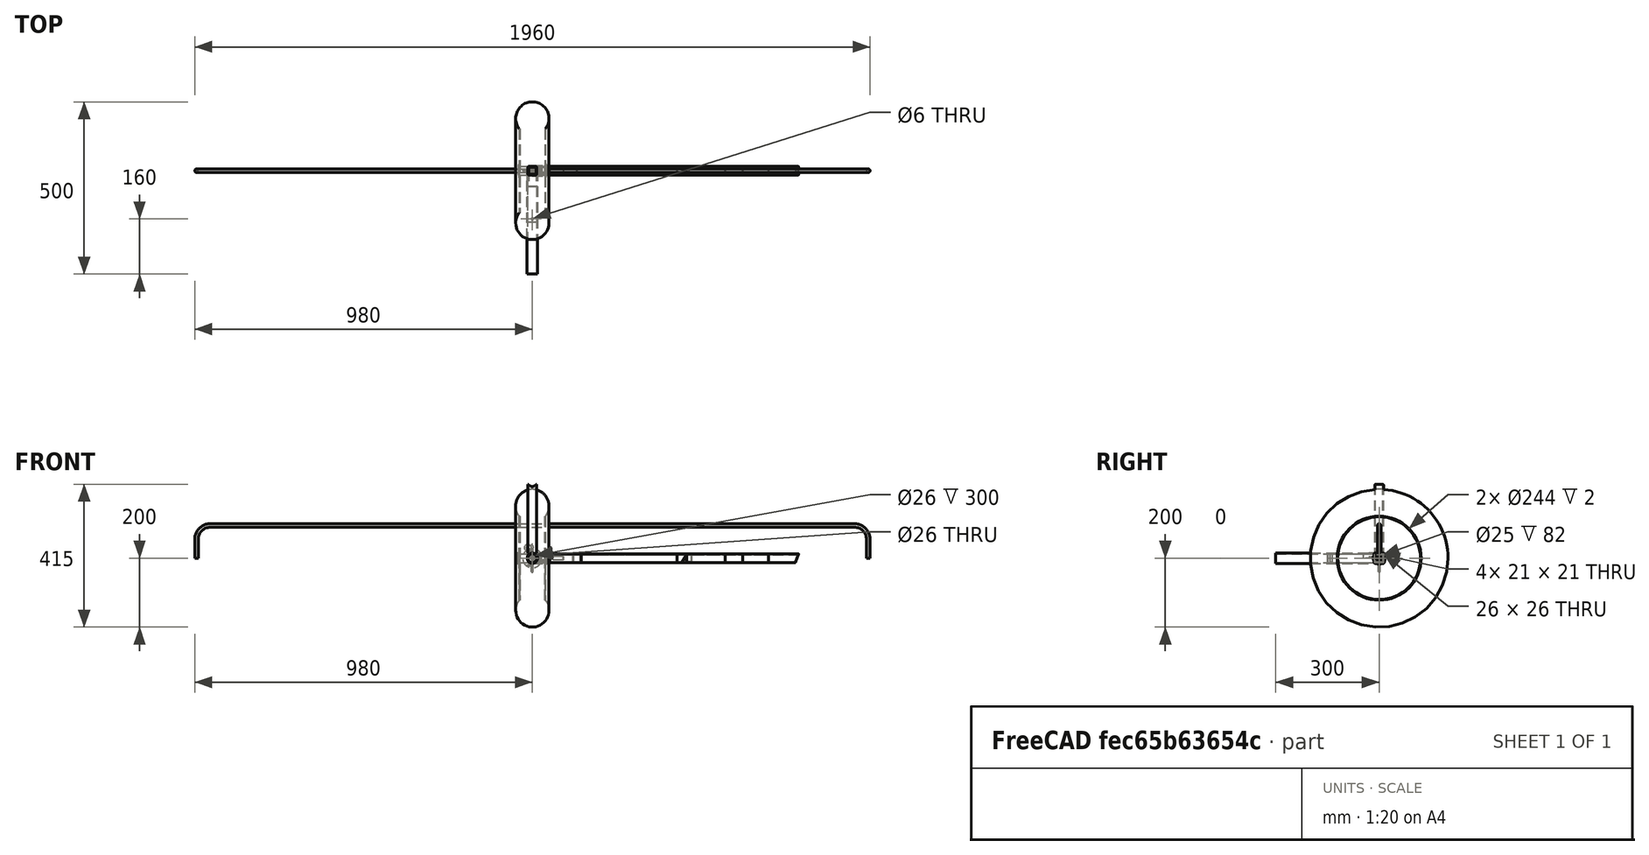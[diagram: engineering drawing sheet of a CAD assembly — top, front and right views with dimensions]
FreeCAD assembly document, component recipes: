
FREECAD ASSEMBLY — COMPONENT RECIPES ("brouetteas4-am")

This assembly document has 25 components, labeled P0..P24 below (a component is one placed body or linked part). 24 of them carry a construction recipe — the FreeCAD feature program that regenerates the part from scratch, quoted from this document or its linked companion documents; the rest are supplied as boundary geometry only. No exploded tour is included for this assembly.
COMPONENT P0 — recipe-attached ("A1", modeled in this document).
Construction recipe (the document's own serialized feature program — sketch geometry with constraints, then the solid features built on it; lengths are millimeters unless a unit is written):

FEATURE [PartDesign::Body] A1005
  AllowCompound = false
  Origin = -> Origin015
COMPONENT P1 — recipe-attached ("A2", modeled in this document).
Construction recipe (the document's own serialized feature program — sketch geometry with constraints, then the solid features built on it; lengths are millimeters unless a unit is written):

FEATURE [PartDesign::Body] Body001
  AllowCompound = false
  Origin = -> Origin004
COMPONENT P2 — recipe-attached ("A3", modeled in this document).
Construction recipe (the document's own serialized feature program — sketch geometry with constraints, then the solid features built on it; lengths are millimeters unless a unit is written):

FEATURE [Sketcher::SketchObject] Sketch002
  ArcFitTolerance = 0
  AttachmentSupport = -> [XZ_Plane007]
  FullyConstrained = true
  MakeInternals = false
  MapMode = 5
  Placement = pos=(0,0,0) rot=(1,0,0;1.5708rad)
  expr: .Constraints.longueur = Spreadsheet.B4 - Spreadsheet.B2 * 2 - 10
  expr: Constraints[4] = Spreadsheet.B2
  sketch-geometry (7):
    g0: LineSegment StartX=-975 StartY=0 StartZ=0 EndX=-975 EndY=25 EndZ=0
    g1: LineSegment StartX=975 StartY=8e-16 StartZ=0 EndX=975 EndY=25 EndZ=0
    g2: LineSegment StartX=-975 StartY=25 StartZ=0 EndX=-975 EndY=55 EndZ=0
    g3: LineSegment StartX=-935 StartY=95 StartZ=0 EndX=935 EndY=95 EndZ=0
    g4: LineSegment StartX=975 StartY=55 StartZ=0 EndX=975 EndY=25 EndZ=0
    g5: ArcOfCircle CenterX=935 CenterY=55 CenterZ=0 NormalX=0 NormalY=0 NormalZ=1 AngleXU=0 Radius=40 StartAngle=0 EndAngle=1.5708
    g6: ArcOfCircle CenterX=-935 CenterY=55 CenterZ=0 NormalX=0 NormalY=0 NormalZ=1 AngleXU=0 Radius=40 StartAngle=1.5708 EndAngle=3.14159
  constraints (19):
    c: PointOnObject(g0,g-1)
    c: Vertical(g0)
    c: Vertical(g1)
    c: Symmetric(g0,g1,g-2)
    c: DistanceY(g0,g0) = 25
    c: DistanceX(g0,g1) = 1950  'longueur'
    c: Equal(g1,g0)
    c: Coincident(g0,g2)
    c: Vertical(g2)
    c: Horizontal(g3)
    c: Coincident(g4,g1)
    c: Vertical(g4)
    c: Tangent(g3,g5) = 1.5708
    c: Tangent(g4,g5) = 1.5708
    c: Tangent(g2,g6) = 1.5708
    c: Tangent(g3,g6) = 1.5708
    c: Equal(g6,g5)
    c: DistanceY(g0,g3) = 70
    c: Radius(g6) = 40
FEATURE [Sketcher::SketchObject] Sketch003
  ArcFitTolerance = 0
  AttachmentSupport = -> [XY_Plane007]
  ExternalGeometry = -> [Sketch002]
  FullyConstrained = true
  MakeInternals = false
  MapMode = 5
  sketch-geometry (1):
    g0: Circle CenterX=-975 CenterY=0 CenterZ=0 NormalX=0 NormalY=0 NormalZ=1 AngleXU=0 Radius=5
  constraints (2):
    c: Coincident(g0,g-3)
    c: Diameter(g0) = 10
FEATURE [PartDesign::AdditivePipe] AdditivePipe
  AuxilleryCurvelinear = true
  AuxillerySpineTangent = false
  Binormal = (0,0,0)
  Mode = 0
  Profile = -> Sketch003
  Spine = -> Sketch002
  SpineTangent = false
  Suppressed = false
  Transformation = 0
  Transition = 0
FEATURE [PartDesign::Body] Body002
  AllowCompound = false
  Group = -> [Sketch002,Sketch003,AdditivePipe]
  Origin = -> Origin007
  Tip = -> AdditivePipe
COMPONENT P3 — recipe-attached ("A4", modeled in this document).
Construction recipe (the document's own serialized feature program — sketch geometry with constraints, then the solid features built on it; lengths are millimeters unless a unit is written):

FEATURE [Sketcher::SketchObject] Sketch004
  ArcFitTolerance = 0
  AttachmentSupport = -> [YZ_Plane008]
  FullyConstrained = true
  MakeInternals = false
  MapMode = 5
  Placement = pos=(0,0,0) rot=(0.57735,0.57735,0.57735;2.0944rad)
  sketch-geometry (1):
    g0: Circle CenterX=0 CenterY=0 CenterZ=0 NormalX=0 NormalY=0 NormalZ=1 AngleXU=0 Radius=5
  constraints (2):
    c: Coincident(g0,g-1)
    c: Diameter(g0) = 10  'diametre'
FEATURE [PartDesign::Pad] Pad002
  Direction = (1,0,0)
  Length = 90
  Length2 = 100
  Placement = pos=(0,0,0) rot=(0.57735,0.57735,0.57735;2.0944rad)
  Profile = -> Sketch004
  Suppressed = false
  Type = 0
FEATURE [PartDesign::Body] Body003
  AllowCompound = false
  Group = -> [Sketch004,Pad002]
  Origin = -> Origin008
  Tip = -> Pad002
COMPONENT P4 — recipe-attached ("A5", modeled in this document).
Construction recipe (the document's own serialized feature program — sketch geometry with constraints, then the solid features built on it; lengths are millimeters unless a unit is written):

FEATURE [PartDesign::Body] Body005
  AllowCompound = false
  Origin = -> Origin012
COMPONENT P5 — recipe-attached ("A6", modeled in this document).
Construction recipe (the document's own serialized feature program — sketch geometry with constraints, then the solid features built on it; lengths are millimeters unless a unit is written):

FEATURE [Sketcher::SketchObject] Sketch008
  ArcFitTolerance = 0
  FullyConstrained = true
  MakeInternals = false
  MapMode = 2
  Placement = pos=(0,0,0) rot=(0.57735,0.57735,0.57735;2.0944rad)
  expr: Constraints[15] = .Constraints.hauteur * 0.1
  expr: Constraints[27] = .Constraints.epaisseur
  sketch-geometry (12):
    g0: LineSegment StartX=-10 StartY=12.5 StartZ=0 EndX=10 EndY=12.5 EndZ=0
    g1: LineSegment StartX=12.5 StartY=10 StartZ=0 EndX=12.5 EndY=-10 EndZ=0
    g2: LineSegment StartX=10 StartY=-12.5 StartZ=0 EndX=-10 EndY=-12.5 EndZ=0
    g3: LineSegment StartX=-12.5 StartY=-10 StartZ=0 EndX=-12.5 EndY=10 EndZ=0
    g4: ArcOfCircle CenterX=-10 CenterY=10 CenterZ=0 NormalX=0 NormalY=0 NormalZ=1 AngleXU=0 Radius=2.5 StartAngle=1.5708 EndAngle=3.14159
    g5: ArcOfCircle CenterX=10 CenterY=10 CenterZ=0 NormalX=0 NormalY=0 NormalZ=1 AngleXU=0 Radius=2.5 StartAngle=2e-16 EndAngle=1.5708
    g6: ArcOfCircle CenterX=10 CenterY=-10 CenterZ=0 NormalX=0 NormalY=0 NormalZ=1 AngleXU=0 Radius=2.5 StartAngle=4.71239 EndAngle=6.28319
    g7: ArcOfCircle CenterX=-10 CenterY=-10 CenterZ=0 NormalX=0 NormalY=0 NormalZ=1 AngleXU=0 Radius=2.5 StartAngle=3.14159 EndAngle=4.71239
    g8: LineSegment StartX=-10.5 StartY=10.5 StartZ=0 EndX=10.5 EndY=10.5 EndZ=0
    g9: LineSegment StartX=10.5 StartY=10.5 StartZ=0 EndX=10.5 EndY=-10.5 EndZ=0
    g10: LineSegment StartX=10.5 StartY=-10.5 StartZ=0 EndX=-10.5 EndY=-10.5 EndZ=0
    g11: LineSegment StartX=-10.5 StartY=-10.5 StartZ=0 EndX=-10.5 EndY=10.5 EndZ=0
  constraints (28):
    c: Horizontal(g2)
    c: Vertical(g3)
    c: Tangent(g0,g4) = 1.5708
    c: Tangent(g3,g4) = 1.5708
    c: Tangent(g0,g5) = 1.5708
    c: Tangent(g1,g5) = 1.5708
    c: Tangent(g1,g6) = 1.5708
    c: Tangent(g2,g6) = 1.5708
    c: Tangent(g2,g7) = 1.5708
    c: Tangent(g3,g7) = 1.5708
    c: Equal(g4,g5)
    c: DistanceY(g2,g0) = 25  'hauteur'
    c: DistanceX(g3,g1) = 25  'largeur'
    c: Equal(g5,g6)
    c: Equal(g6,g7)
    c: Radius(g7) = 2.5
    c: Symmetric(g1,g1,g-1)
    c: Symmetric(g0,g0,g-2)
    c: Coincident(g8,g9)
    c: Coincident(g9,g10)
    c: Coincident(g10,g11)
    c: Coincident(g11,g8)
    c: Horizontal(g10)
    c: Vertical(g11)
    c: Symmetric(g8,g9,g-1)
    c: Symmetric(g8,g8,g-2)
    c: DistanceX(g3,g8) = 2  'epaisseur'
    c: DistanceY(g2,g9) = 2
FEATURE [PartDesign::Pad] Pad004
  Direction = (1,1e-16,-1e-16)
  Length = 420
  Length2 = 100
  Placement = pos=(0,0,0) rot=(0.57735,0.57735,0.57735;2.0944rad)
  Profile = -> Sketch008
  Suppressed = false
  Type = 0
  expr: Length = Spreadsheet.D4 - Spreadsheet.B9 * 2
FEATURE [PartDesign::Body] Body006
  AllowCompound = false
  Group = -> [Sketch008,Pad004]
  Origin = -> Origin014
  Tip = -> Pad004
COMPONENT P6 — recipe-attached ("A7", modeled in this document).
Construction recipe (the document's own serialized feature program — sketch geometry with constraints, then the solid features built on it; lengths are millimeters unless a unit is written):

FEATURE [PartDesign::Body] A7002
  AllowCompound = false
COMPONENT P7 — recipe-attached ("A8", modeled in this document).
Construction recipe (the document's own serialized feature program — sketch geometry with constraints, then the solid features built on it; lengths are millimeters unless a unit is written):

FEATURE [PartDesign::CoordinateSystem] LCS_0013
  AttacherType = Attacher::AttachEngine3D
  AttachmentSupport = -> [X_Axis020]
  MapMode = 2
FEATURE [PartDesign::Body] A8001
  AllowCompound = false
  Group = -> [LCS_0013]
  Origin = -> Origin018
COMPONENT P8 — recipe-attached ("A9", modeled in this document).
Construction recipe (the document's own serialized feature program — sketch geometry with constraints, then the solid features built on it; lengths are millimeters unless a unit is written):

FEATURE [Sketcher::SketchObject] Sketch011
  ArcFitTolerance = 0
  FullyConstrained = true
  MakeInternals = false
  MapMode = 5
  expr: Constraints[15] = .Constraints.hauteur * 0.1
  expr: Constraints[27] = .Constraints.epaisseur
  sketch-geometry (12):
    g0: LineSegment StartX=-10 StartY=12.5 StartZ=0 EndX=10 EndY=12.5 EndZ=0
    g1: LineSegment StartX=12.5 StartY=10 StartZ=0 EndX=12.5 EndY=-10 EndZ=0
    g2: LineSegment StartX=10 StartY=-12.5 StartZ=0 EndX=-10 EndY=-12.5 EndZ=0
    g3: LineSegment StartX=-12.5 StartY=-10 StartZ=0 EndX=-12.5 EndY=10 EndZ=0
    g4: ArcOfCircle CenterX=-10 CenterY=10 CenterZ=0 NormalX=0 NormalY=0 NormalZ=1 AngleXU=0 Radius=2.5 StartAngle=1.5708 EndAngle=3.14159
    g5: ArcOfCircle CenterX=10 CenterY=10 CenterZ=0 NormalX=0 NormalY=0 NormalZ=1 AngleXU=0 Radius=2.5 StartAngle=2e-16 EndAngle=1.5708
    g6: ArcOfCircle CenterX=10 CenterY=-10 CenterZ=0 NormalX=0 NormalY=0 NormalZ=1 AngleXU=0 Radius=2.5 StartAngle=4.71239 EndAngle=6.28319
    g7: ArcOfCircle CenterX=-10 CenterY=-10 CenterZ=0 NormalX=0 NormalY=0 NormalZ=1 AngleXU=0 Radius=2.5 StartAngle=3.14159 EndAngle=4.71239
    g8: LineSegment StartX=-10.5 StartY=10.5 StartZ=0 EndX=10.5 EndY=10.5 EndZ=0
    g9: LineSegment StartX=10.5 StartY=10.5 StartZ=0 EndX=10.5 EndY=-10.5 EndZ=0
    g10: LineSegment StartX=10.5 StartY=-10.5 StartZ=0 EndX=-10.5 EndY=-10.5 EndZ=0
    g11: LineSegment StartX=-10.5 StartY=-10.5 StartZ=0 EndX=-10.5 EndY=10.5 EndZ=0
  constraints (28):
    c: Horizontal(g2)
    c: Vertical(g3)
    c: Tangent(g0,g4) = 1.5708
    c: Tangent(g3,g4) = 1.5708
    c: Tangent(g0,g5) = 1.5708
    c: Tangent(g1,g5) = 1.5708
    c: Tangent(g1,g6) = 1.5708
    c: Tangent(g2,g6) = 1.5708
    c: Tangent(g2,g7) = 1.5708
    c: Tangent(g3,g7) = 1.5708
    c: Equal(g4,g5)
    c: DistanceY(g2,g0) = 25  'hauteur'
    c: DistanceX(g3,g1) = 25  'largeur'
    c: Equal(g5,g6)
    c: Equal(g6,g7)
    c: Radius(g7) = 2.5
    c: Symmetric(g1,g1,g-1)
    c: Symmetric(g0,g0,g-2)
    c: Coincident(g8,g9)
    c: Coincident(g9,g10)
    c: Coincident(g10,g11)
    c: Coincident(g11,g8)
    c: Horizontal(g10)
    c: Vertical(g11)
    c: Symmetric(g8,g9,g-1)
    c: Symmetric(g8,g8,g-2)
    c: DistanceX(g3,g8) = 2  'epaisseur'
    c: DistanceY(g2,g9) = 2
FEATURE [PartDesign::Pad] Pad007
  Direction = (0,0,1)
  Length = 215
  Length2 = 100
  Profile = -> Sketch011
  Suppressed = false
  Type = 0
  expr: Length = Spreadsheet.B11 - Spreadsheet.B5 - Spreadsheet.B2 * 2
FEATURE [PartDesign::CoordinateSystem] LCS_0014
  AttacherType = Attacher::AttachEngine3D
  AttachmentSupport = -> [X_Axis021]
  MapMode = 2
FEATURE [Sketcher::SketchObject] Sketch023
  ArcFitTolerance = 0
  AttachmentSupport = -> [Pad007]
  ExternalGeometry = -> [Pad007]
  FullyConstrained = true
  MakeInternals = false
  MapMode = 5
  Placement = pos=(0,-12.5,0) rot=(1,0,0;1.5708rad)
  expr: Constraints[0] = Spreadsheet.B13
  sketch-geometry (1):
    g0: Circle CenterX=0 CenterY=223.292 CenterZ=0 NormalX=0 NormalY=0 NormalZ=1 AngleXU=0 Radius=15
  constraints (4):
    c: Diameter(g0) = 30
    c: PointOnObject(g0,g-2)
    c: PointOnObject(g-4,g0)
    c: DistanceY(g-4,g0) = 8.29156  'deport'
FEATURE [PartDesign::Pocket] Pocket
  BaseFeature = -> Pad007
  Direction = (0,1,-2e-16)
  Length = 5
  Length2 = 100
  Profile = -> Sketch023
  Suppressed = false
  Type = 1
FEATURE [PartDesign::Body] A8004
  AllowCompound = false
  Group = -> [LCS_0014,Pad007,Sketch011,Sketch023,Pocket]
  Origin = -> Origin020
  Tip = -> Pocket
COMPONENT P9 — geometry summary ("Model"; no construction recipe available for this part):
  bounding box: 2615.0 x 1122.2 x 688.0 mm
  tessellated surface: 4,540 triangles
  volume: 21124853 mm^3 (1% of its bounding box)
  symmetry: mirror-symmetric across its y mid-plane
COMPONENT P10 — recipe-attached ("A10", modeled in this document).
Construction recipe (the document's own serialized feature program — sketch geometry with constraints, then the solid features built on it; lengths are millimeters unless a unit is written):

FEATURE [Sketcher::SketchObject] Sketch012
  ArcFitTolerance = 0
  AttachmentSupport = -> [XZ_Plane022]
  FullyConstrained = true
  MakeInternals = false
  MapMode = 5
  Placement = pos=(0,0,0) rot=(1,0,0;1.5708rad)
  sketch-geometry (1):
    g0: Circle CenterX=0 CenterY=0 CenterZ=0 NormalX=0 NormalY=0 NormalZ=1 AngleXU=0 Radius=12.5
  constraints (2):
    c: Coincident(g0,g-1)
    c: Diameter(g0) = 25  'diametre'
FEATURE [PartDesign::Pad] Pad008
  Direction = (0,-1,2e-16)
  Length = 150
  Length2 = 100
  Placement = pos=(0,0,0) rot=(1,0,0;1.5708rad)
  Profile = -> Sketch012
  Suppressed = false
  Type = 0
FEATURE [PartDesign::Plane] DatumPlane004
  AttachmentOffset = pos=(0,0,12.5) rot=(0,0,1;0rad)
  AttachmentSupport = -> [XY_Plane022]
  Length = 68.7083
  MapMode = 5
  Placement = pos=(0,0,12.5) rot=(0,0,1;0rad)
  ResizeMode = 0
  Width = 193.708
FEATURE [Sketcher::SketchObject] Sketch034
  ArcFitTolerance = 1e-06
  AttachmentSupport = -> [DatumPlane004]
  FullyConstrained = false
  MakeInternals = false
  MapMode = 5
  Placement = pos=(0,0,12.5) rot=(0,0,1;0rad)
  expr: Constraints[0] = Pad008.Length - 10 mm
  sketch-geometry (1):
    g0: Circle CenterX=0 CenterY=-140 CenterZ=0 NormalX=0 NormalY=0 NormalZ=1 AngleXU=0 Radius=16.367
  constraints (2):
    c: DistanceY(g0,g-1) = 140
    c: PointOnObject(g0,g-2)
FEATURE [PartDesign::Hole] Hole
  BaseFeature = -> Pad008
  CustomThreadClearance = 0
  Depth = 326.607
  DepthType = 1
  Diameter = 6
  DrillForDepth = false
  DrillPoint = 1
  DrillPointAngle = 118
  HoleCutCountersinkAngle = 90
  HoleCutCustomValues = false
  HoleCutDepth = 0
  HoleCutDiameter = 6.1
  HoleCutType = 0
  ModelThread = false
  Placement = pos=(0,0,0) rot=(1,0,0;1.5708rad)
  Profile = -> Sketch034
  Suppressed = false
  Tapered = false
  TaperedAngle = 90
  ThreadClass = 0
  ThreadDepth = 326.607
  ThreadDepthType = 0
  ThreadDirection = 0
  ThreadFit = 0
  ThreadSize = 0
  ThreadType = 0
  Threaded = false
  UseCustomThreadClearance = false
FEATURE [PartDesign::Body] Body
  AllowCompound = false
  Group = -> [Sketch012,Pad008,Sketch034,DatumPlane004,Hole]
  Origin = -> Origin022
  Tip = -> Hole
COMPONENT P11 — recipe-attached ("A11", modeled in this document).
Construction recipe (the document's own serialized feature program — sketch geometry with constraints, then the solid features built on it; lengths are millimeters unless a unit is written):

FEATURE [Sketcher::SketchObject] Sketch013
  ArcFitTolerance = 0
  AttachmentSupport = -> [XZ_Plane024]
  FullyConstrained = true
  MakeInternals = false
  MapMode = 5
  Placement = pos=(0,0,0) rot=(1,0,0;1.5708rad)
  expr: Constraints[22] = .Constraints.epaisseur
  expr: Constraints[24] = .Constraints.largeur * 20 / 100
  sketch-geometry (10):
    g0: LineSegment StartX=-15 StartY=15 StartZ=0 EndX=-15 EndY=0 EndZ=0
    g1: LineSegment StartX=-15 StartY=0 StartZ=0 EndX=15 EndY=0 EndZ=0
    g2: LineSegment StartX=15 StartY=0 StartZ=0 EndX=15 EndY=15 EndZ=0
    g3: LineSegment StartX=15 StartY=15 StartZ=0 EndX=14 EndY=15 EndZ=0
    g4: LineSegment StartX=11 StartY=12 StartZ=0 EndX=11 EndY=4 EndZ=0
    g5: LineSegment StartX=11 StartY=4 StartZ=0 EndX=-11 EndY=4 EndZ=0
    g6: LineSegment StartX=-11 StartY=4 StartZ=0 EndX=-11 EndY=12 EndZ=0
    g7: LineSegment StartX=-14 StartY=15 StartZ=0 EndX=-15 EndY=15 EndZ=0
    g8: ArcOfCircle CenterX=-14 CenterY=12 CenterZ=0 NormalX=0 NormalY=0 NormalZ=1 AngleXU=0 Radius=3 StartAngle=0 EndAngle=1.5708
    g9: ArcOfCircle CenterX=14 CenterY=12 CenterZ=0 NormalX=0 NormalY=0 NormalZ=1 AngleXU=0 Radius=3 StartAngle=1.5708 EndAngle=3.14159
  constraints (25):
    c: PointOnObject(g0,g-1)
    c: Vertical(g0)
    c: Coincident(g0,g1)
    c: Coincident(g1,g2)
    c: Coincident(g2,g3)
    c: Horizontal(g3)
    c: Vertical(g4)
    c: Coincident(g4,g5)
    c: Coincident(g5,g6)
    c: Coincident(g7,g0)
    c: Horizontal(g7)
    c: Symmetric(g1,g0,g-2)
    c: Symmetric(g5,g4,g-2)
    c: Tangent(g6,g8) = -1.5708
    c: Tangent(g7,g8) = -1.5708
    c: Tangent(g3,g9) = -1.5708
    c: Tangent(g4,g9) = -1.5708
    c: Equal(g8,g9)
    c: Symmetric(g0,g2,g-2)
    c: Vertical(g6)
    c: DistanceX(g1,g1) = 30  'largeur'
    c: DistanceY(g2,g2) = 15  'hauteur'
    c: DistanceY(g1,g4) = 4
    c: DistanceX(g4,g1) = 4  'epaisseur'
    c: Diameter(g8) = 6
FEATURE [PartDesign::Pad] Pad009
  Direction = (0,-1,2e-16)
  Length = 46
  Length2 = 100
  Placement = pos=(0,0,0) rot=(1,0,0;1.5708rad)
  Profile = -> Sketch013
  Suppressed = false
  Type = 0
FEATURE [PartDesign::Body] Body007
  AllowCompound = false
  Group = -> [Sketch013,Pad009]
  Origin = -> Origin024
  Tip = -> Pad009
COMPONENT P12 — recipe-attached ("A12", modeled in this document).
Construction recipe (the document's own serialized feature program — sketch geometry with constraints, then the solid features built on it; lengths are millimeters unless a unit is written):

FEATURE [PartDesign::Body] Body008
  AllowCompound = false
  Origin = -> Origin028
COMPONENT P13 — recipe-attached ("A13", modeled in this document).
Construction recipe (the document's own serialized feature program — sketch geometry with constraints, then the solid features built on it; lengths are millimeters unless a unit is written):

FEATURE [Sketcher::SketchObject] Sketch016
  ArcFitTolerance = 0
  FullyConstrained = true
  MakeInternals = false
  MapMode = 5
  Placement = pos=(0,0,0) rot=(0.57735,0.57735,0.57735;2.0944rad)
  expr: Constraints[15] = .Constraints.hauteur * 0.1
  expr: Constraints[27] = .Constraints.epaisseur
  sketch-geometry (12):
    g0: LineSegment StartX=-10 StartY=12.5 StartZ=0 EndX=10 EndY=12.5 EndZ=0
    g1: LineSegment StartX=12.5 StartY=10 StartZ=0 EndX=12.5 EndY=-10 EndZ=0
    g2: LineSegment StartX=10 StartY=-12.5 StartZ=0 EndX=-10 EndY=-12.5 EndZ=0
    g3: LineSegment StartX=-12.5 StartY=-10 StartZ=0 EndX=-12.5 EndY=10 EndZ=0
    g4: ArcOfCircle CenterX=-10 CenterY=10 CenterZ=0 NormalX=0 NormalY=0 NormalZ=1 AngleXU=0 Radius=2.5 StartAngle=1.5708 EndAngle=3.14159
    g5: ArcOfCircle CenterX=10 CenterY=10 CenterZ=0 NormalX=0 NormalY=0 NormalZ=1 AngleXU=0 Radius=2.5 StartAngle=2e-16 EndAngle=1.5708
    g6: ArcOfCircle CenterX=10 CenterY=-10 CenterZ=0 NormalX=0 NormalY=0 NormalZ=1 AngleXU=0 Radius=2.5 StartAngle=4.71239 EndAngle=6.28319
    g7: ArcOfCircle CenterX=-10 CenterY=-10 CenterZ=0 NormalX=0 NormalY=0 NormalZ=1 AngleXU=0 Radius=2.5 StartAngle=3.14159 EndAngle=4.71239
    g8: LineSegment StartX=-10.5 StartY=10.5 StartZ=0 EndX=10.5 EndY=10.5 EndZ=0
    g9: LineSegment StartX=10.5 StartY=10.5 StartZ=0 EndX=10.5 EndY=-10.5 EndZ=0
    g10: LineSegment StartX=10.5 StartY=-10.5 StartZ=0 EndX=-10.5 EndY=-10.5 EndZ=0
    g11: LineSegment StartX=-10.5 StartY=-10.5 StartZ=0 EndX=-10.5 EndY=10.5 EndZ=0
  constraints (28):
    c: Horizontal(g2)
    c: Vertical(g3)
    c: Tangent(g0,g4) = 1.5708
    c: Tangent(g3,g4) = 1.5708
    c: Tangent(g0,g5) = 1.5708
    c: Tangent(g1,g5) = 1.5708
    c: Tangent(g1,g6) = 1.5708
    c: Tangent(g2,g6) = 1.5708
    c: Tangent(g2,g7) = 1.5708
    c: Tangent(g3,g7) = 1.5708
    c: Equal(g4,g5)
    c: DistanceY(g2,g0) = 25  'hauteur'
    c: DistanceX(g3,g1) = 25  'largeur'
    c: Equal(g5,g6)
    c: Equal(g6,g7)
    c: Radius(g7) = 2.5
    c: Symmetric(g1,g1,g-1)
    c: Symmetric(g0,g0,g-2)
    c: Coincident(g8,g9)
    c: Coincident(g9,g10)
    c: Coincident(g10,g11)
    c: Coincident(g11,g8)
    c: Horizontal(g10)
    c: Vertical(g11)
    c: Symmetric(g8,g9,g-1)
    c: Symmetric(g8,g8,g-2)
    c: DistanceX(g3,g8) = 2  'epaisseur'
    c: DistanceY(g2,g9) = 2
FEATURE [PartDesign::Pad] Pad011
  Direction = (1,1e-16,-1e-16)
  Length = 449.646
  Length2 = 100
  Placement = pos=(0,0,0) rot=(0.57735,0.57735,0.57735;2.0944rad)
  Profile = -> Sketch016
  Suppressed = false
  Type = 0
  expr: Length = Sketch014.Constraints.lpied
FEATURE [Sketcher::SketchObject] Sketch028
  ArcFitTolerance = 1e-06
  AttachmentSupport = -> [YZ_Plane029]
  ExternalGeometry = -> [Pad011]
  FullyConstrained = false
  MakeInternals = false
  MapMode = 5
  Placement = pos=(0,0,0) rot=(0.57735,0.57735,0.57735;2.0944rad)
  sketch-geometry (5):
    g0: LineSegment StartX=-17.5 StartY=12.5 StartZ=0 EndX=-17.5 EndY=-57.5 EndZ=0
    g1: LineSegment StartX=-17.5 StartY=-57.5 StartZ=0 EndX=17.5 EndY=-57.5 EndZ=0
    g2: LineSegment StartX=17.5 StartY=-57.5 StartZ=0 EndX=17.5 EndY=12.5 EndZ=0
    g3: LineSegment StartX=17.5 StartY=12.5 StartZ=0 EndX=-17.5 EndY=12.5 EndZ=0
    g4: LineSegment [constr] StartX=-59.8857 StartY=12.5 StartZ=0 EndX=133.957 EndY=12.5 EndZ=0
  constraints (13):
    c: Coincident(g0,g1)
    c: Coincident(g1,g2)
    c: Coincident(g2,g3)
    c: Coincident(g3,g0)
    c: Vertical(g0)
    c: Vertical(g2)
    c: Horizontal(g1)
    c: Horizontal(g4)
    c: PointOnObject(g2,g4)
    c: DistanceX(g1,g1) = 35
    c: DistanceY(g2,g2) = 70
    c: Symmetric(g0,g2,g-2)
    c: PointOnObject(g-3,g4)
FEATURE [PartDesign::Groove] Groove002
  Angle = 56.5107
  Angle2 = 60
  Axis = (0,193.843,0)
  Base = (0,-59.8857,12.5)
  BaseFeature = -> Pad011
  Placement = pos=(0,0,0) rot=(0.57735,0.57735,0.57735;2.0944rad)
  Profile = -> Sketch028
  ReferenceAxis = -> Sketch028 [Axis]
  Reversed = true
  Suppressed = false
  Type = 0
  expr: Angle = 90 ° - Sketch014.Constraints.angle
FEATURE [PartDesign::Plane] DatumPlane001
  AttachmentSupport = -> [Groove002]
  Length = 60
  MapMode = 5
  Placement = pos=(449.646,1.978e-13,0) rot=(0.57735,0.57735,0.57735;2.0944rad)
  ResizeMode = 0
  Width = 60
FEATURE [Sketcher::SketchObject] Sketch029
  ArcFitTolerance = 1e-06
  AttachmentSupport = -> [DatumPlane001]
  ExternalGeometry = -> [Groove002]
  FullyConstrained = false
  MakeInternals = false
  MapMode = 5
  Placement = pos=(449.646,1.978e-13,0) rot=(0.57735,0.57735,0.57735;2.0944rad)
  sketch-geometry (5):
    g0: LineSegment [constr] StartX=-50.285 StartY=12.5 StartZ=0 EndX=61.7161 EndY=12.5 EndZ=0
    g1: LineSegment StartX=-17.5 StartY=12.5 StartZ=0 EndX=-17.5 EndY=-57.5 EndZ=0
    g2: LineSegment StartX=-17.5 StartY=-57.5 StartZ=0 EndX=17.5 EndY=-57.5 EndZ=0
    g3: LineSegment StartX=17.5 StartY=-57.5 StartZ=0 EndX=17.5 EndY=12.5 EndZ=0
    g4: LineSegment StartX=17.5 StartY=12.5 StartZ=0 EndX=-17.5 EndY=12.5 EndZ=0
  constraints (13):
    c: Horizontal(g0)
    c: PointOnObject(g-3,g0)
    c: Coincident(g1,g2)
    c: Coincident(g2,g3)
    c: Coincident(g3,g4)
    c: Coincident(g4,g1)
    c: Vertical(g1)
    c: Vertical(g3)
    c: Horizontal(g2)
    c: Distance(g1,g3) = 35
    c: Distance(g2,g4) = 70
    c: PointOnObject(g1,g0)
    c: Symmetric(g3,g1,g-2)
FEATURE [PartDesign::Groove] Groove003
  Angle = 33.4893
  Angle2 = 60
  Axis = (-1.492e-13,112.001,0)
  Base = (449.646,-50.285,12.5)
  BaseFeature = -> Groove002
  Placement = pos=(0,0,0) rot=(0.57735,0.57735,0.57735;2.0944rad)
  Profile = -> Sketch029
  ReferenceAxis = -> Sketch029 [Axis]
  Suppressed = false
  Type = 0
  expr: Angle = Sketch014.Constraints.angle
FEATURE [PartDesign::Body] Body009
  AllowCompound = false
  Group = -> [Sketch016,Pad011,Sketch028,Groove002,DatumPlane001,Sketch029,Groove003]
  Origin = -> Origin029
  Tip = -> Groove003
COMPONENT P14 — recipe-attached ("A14", modeled in this document).
Construction recipe (the document's own serialized feature program — sketch geometry with constraints, then the solid features built on it; lengths are millimeters unless a unit is written):

FEATURE [Sketcher::SketchObject] Sketch017
  ArcFitTolerance = 0
  FullyConstrained = true
  MakeInternals = false
  MapMode = 5
  Placement = pos=(0,0,0) rot=(0.57735,0.57735,0.57735;2.0944rad)
  expr: Constraints[15] = .Constraints.hauteur * 0.1
  expr: Constraints[27] = .Constraints.epaisseur
  sketch-geometry (12):
    g0: LineSegment StartX=-10 StartY=12.5 StartZ=0 EndX=10 EndY=12.5 EndZ=0
    g1: LineSegment StartX=12.5 StartY=10 StartZ=0 EndX=12.5 EndY=-10 EndZ=0
    g2: LineSegment StartX=10 StartY=-12.5 StartZ=0 EndX=-10 EndY=-12.5 EndZ=0
    g3: LineSegment StartX=-12.5 StartY=-10 StartZ=0 EndX=-12.5 EndY=10 EndZ=0
    g4: ArcOfCircle CenterX=-10 CenterY=10 CenterZ=0 NormalX=0 NormalY=0 NormalZ=1 AngleXU=0 Radius=2.5 StartAngle=1.5708 EndAngle=3.14159
    g5: ArcOfCircle CenterX=10 CenterY=10 CenterZ=0 NormalX=0 NormalY=0 NormalZ=1 AngleXU=0 Radius=2.5 StartAngle=2e-16 EndAngle=1.5708
    g6: ArcOfCircle CenterX=10 CenterY=-10 CenterZ=0 NormalX=0 NormalY=0 NormalZ=1 AngleXU=0 Radius=2.5 StartAngle=4.71239 EndAngle=6.28319
    g7: ArcOfCircle CenterX=-10 CenterY=-10 CenterZ=0 NormalX=0 NormalY=0 NormalZ=1 AngleXU=0 Radius=2.5 StartAngle=3.14159 EndAngle=4.71239
    g8: LineSegment StartX=-10.5 StartY=10.5 StartZ=0 EndX=10.5 EndY=10.5 EndZ=0
    g9: LineSegment StartX=10.5 StartY=10.5 StartZ=0 EndX=10.5 EndY=-10.5 EndZ=0
    g10: LineSegment StartX=10.5 StartY=-10.5 StartZ=0 EndX=-10.5 EndY=-10.5 EndZ=0
    g11: LineSegment StartX=-10.5 StartY=-10.5 StartZ=0 EndX=-10.5 EndY=10.5 EndZ=0
  constraints (28):
    c: Horizontal(g2)
    c: Vertical(g3)
    c: Tangent(g0,g4) = 1.5708
    c: Tangent(g3,g4) = 1.5708
    c: Tangent(g0,g5) = 1.5708
    c: Tangent(g1,g5) = 1.5708
    c: Tangent(g1,g6) = 1.5708
    c: Tangent(g2,g6) = 1.5708
    c: Tangent(g2,g7) = 1.5708
    c: Tangent(g3,g7) = 1.5708
    c: Equal(g4,g5)
    c: DistanceY(g2,g0) = 25  'hauteur'
    c: DistanceX(g3,g1) = 25  'largeur'
    c: Equal(g5,g6)
    c: Equal(g6,g7)
    c: Radius(g7) = 2.5
    c: Symmetric(g1,g1,g-1)
    c: Symmetric(g0,g0,g-2)
    c: Coincident(g8,g9)
    c: Coincident(g9,g10)
    c: Coincident(g10,g11)
    c: Coincident(g11,g8)
    c: Horizontal(g10)
    c: Vertical(g11)
    c: Symmetric(g8,g9,g-1)
    c: Symmetric(g8,g8,g-2)
    c: DistanceX(g3,g8) = 2  'epaisseur'
    c: DistanceY(g2,g9) = 2
FEATURE [PartDesign::Pad] Pad012
  Direction = (1,1e-16,-1e-16)
  Length = 772.835
  Length2 = 100
  Placement = pos=(0,0,0) rot=(0.57735,0.57735,0.57735;2.0944rad)
  Profile = -> Sketch017
  ReferenceAxis = -> Sketch017 [N_Axis]
  Suppressed = false
  Type = 0
  expr: Length = Sketch014.Constraints.ldiag + Sketch014.Constraints.rajoueroue
FEATURE [Sketcher::SketchObject] Sketch032
  ArcFitTolerance = 1e-06
  AttachmentSupport = -> [YZ_Plane030]
  ExternalGeometry = -> [Pad012]
  FullyConstrained = false
  MakeInternals = false
  MapMode = 5
  Placement = pos=(0,0,0) rot=(0.57735,0.57735,0.57735;2.0944rad)
  sketch-geometry (5):
    g0: LineSegment StartX=17.5 StartY=57.5 StartZ=0 EndX=-17.5 EndY=57.5 EndZ=0
    g1: LineSegment StartX=-17.5 StartY=57.5 StartZ=0 EndX=-17.5 EndY=-12.5 EndZ=0
    g2: LineSegment StartX=-17.5 StartY=-12.5 StartZ=0 EndX=17.5 EndY=-12.5 EndZ=0
    g3: LineSegment StartX=17.5 StartY=-12.5 StartZ=0 EndX=17.5 EndY=57.5 EndZ=0
    g4: LineSegment [constr] StartX=69.7742 StartY=-12.5 StartZ=0 EndX=-82.9271 EndY=-12.5 EndZ=0
  constraints (13):
    c: Coincident(g0,g1)
    c: Coincident(g1,g2)
    c: Coincident(g2,g3)
    c: Coincident(g3,g0)
    c: Horizontal(g0)
    c: Vertical(g1)
    c: Vertical(g3)
    c: Distance(g1,g3) = 35
    c: Distance(g0,g2) = 70
    c: Symmetric(g1,g2,g-2)
    c: PointOnObject(g1,g-3)
    c: Horizontal(g4)
    c: PointOnObject(g2,g4)
FEATURE [PartDesign::Groove] Groove006
  Angle = 19.6557
  Angle2 = 60
  Axis = (0,-152.701,0)
  Base = (0,69.7742,-12.5)
  BaseFeature = -> Pad012
  Placement = pos=(0,0,0) rot=(0.57735,0.57735,0.57735;2.0944rad)
  Profile = -> Sketch032
  ReferenceAxis = -> Sketch032 [Axis]
  Reversed = true
  Suppressed = false
  Type = 0
  expr: Angle = 90 ° - Sketch014.Constraints.anglerou
FEATURE [PartDesign::Plane] DatumPlane003
  AttachmentSupport = -> [Groove006]
  Length = 60
  MapMode = 5
  Placement = pos=(772.835,3.4e-13,0) rot=(0.57735,0.57735,0.57735;2.0944rad)
  ResizeMode = 0
  Width = 60
FEATURE [Sketcher::SketchObject] Sketch033
  ArcFitTolerance = 1e-06
  AttachmentSupport = -> [DatumPlane003]
  ExternalGeometry = -> [Groove006]
  FullyConstrained = false
  MakeInternals = false
  MapMode = 5
  Placement = pos=(772.835,3.4e-13,0) rot=(0.57735,0.57735,0.57735;2.0944rad)
  sketch-geometry (5):
    g0: LineSegment [constr] StartX=-118.894 StartY=12.5 StartZ=0 EndX=112.379 EndY=12.5 EndZ=0
    g1: LineSegment StartX=-17.5 StartY=12.5 StartZ=0 EndX=-17.5 EndY=-57.5 EndZ=0
    g2: LineSegment StartX=-17.5 StartY=-57.5 StartZ=0 EndX=17.5 EndY=-57.5 EndZ=0
    g3: LineSegment StartX=17.5 StartY=-57.5 StartZ=0 EndX=17.5 EndY=12.5 EndZ=0
    g4: LineSegment StartX=17.5 StartY=12.5 StartZ=0 EndX=-17.5 EndY=12.5 EndZ=0
  constraints (13):
    c: Horizontal(g0)
    c: Coincident(g1,g2)
    c: Coincident(g2,g3)
    c: Coincident(g3,g4)
    c: Coincident(g4,g1)
    c: Vertical(g1)
    c: Vertical(g3)
    c: Horizontal(g2)
    c: Distance(g1,g3) = 35
    c: Distance(g2,g4) = 70
    c: PointOnObject(g1,g0)
    c: Symmetric(g3,g1,g-2)
    c: PointOnObject(g-3,g0)
FEATURE [PartDesign::Groove] Groove007
  Angle = 19.66
  Angle2 = 60
  Axis = (-3.081e-13,231.273,0)
  Base = (772.835,-118.894,12.5)
  BaseFeature = -> Groove006
  Placement = pos=(0,0,0) rot=(0.57735,0.57735,0.57735;2.0944rad)
  Profile = -> Sketch033
  ReferenceAxis = -> Sketch033 [Axis]
  Suppressed = false
  Type = 0
FEATURE [PartDesign::Body] Body010
  AllowCompound = false
  Group = -> [Sketch017,Pad012,Sketch032,Groove006,DatumPlane003,Sketch033,Groove007]
  Origin = -> Origin030
  Tip = -> Groove007
COMPONENT P15 — recipe-attached ("A15", modeled in this document).
Construction recipe (the document's own serialized feature program — sketch geometry with constraints, then the solid features built on it; lengths are millimeters unless a unit is written):

FEATURE [Sketcher::SketchObject] Sketch018
  ArcFitTolerance = 0
  FullyConstrained = true
  MakeInternals = false
  MapMode = 5
  Placement = pos=(0,0,0) rot=(0.57735,0.57735,0.57735;2.0944rad)
  expr: Constraints[15] = .Constraints.hauteur * 0.1
  expr: Constraints[27] = .Constraints.epaisseur
  sketch-geometry (12):
    g0: LineSegment StartX=-10 StartY=12.5 StartZ=0 EndX=10 EndY=12.5 EndZ=0
    g1: LineSegment StartX=12.5 StartY=10 StartZ=0 EndX=12.5 EndY=-10 EndZ=0
    g2: LineSegment StartX=10 StartY=-12.5 StartZ=0 EndX=-10 EndY=-12.5 EndZ=0
    g3: LineSegment StartX=-12.5 StartY=-10 StartZ=0 EndX=-12.5 EndY=10 EndZ=0
    g4: ArcOfCircle CenterX=-10 CenterY=10 CenterZ=0 NormalX=0 NormalY=0 NormalZ=1 AngleXU=0 Radius=2.5 StartAngle=1.5708 EndAngle=3.14159
    g5: ArcOfCircle CenterX=10 CenterY=10 CenterZ=0 NormalX=0 NormalY=0 NormalZ=1 AngleXU=0 Radius=2.5 StartAngle=2e-16 EndAngle=1.5708
    g6: ArcOfCircle CenterX=10 CenterY=-10 CenterZ=0 NormalX=0 NormalY=0 NormalZ=1 AngleXU=0 Radius=2.5 StartAngle=4.71239 EndAngle=6.28319
    g7: ArcOfCircle CenterX=-10 CenterY=-10 CenterZ=0 NormalX=0 NormalY=0 NormalZ=1 AngleXU=0 Radius=2.5 StartAngle=3.14159 EndAngle=4.71239
    g8: LineSegment StartX=-10.5 StartY=10.5 StartZ=0 EndX=10.5 EndY=10.5 EndZ=0
    g9: LineSegment StartX=10.5 StartY=10.5 StartZ=0 EndX=10.5 EndY=-10.5 EndZ=0
    g10: LineSegment StartX=10.5 StartY=-10.5 StartZ=0 EndX=-10.5 EndY=-10.5 EndZ=0
    g11: LineSegment StartX=-10.5 StartY=-10.5 StartZ=0 EndX=-10.5 EndY=10.5 EndZ=0
  constraints (28):
    c: Horizontal(g2)
    c: Vertical(g3)
    c: Tangent(g0,g4) = 1.5708
    c: Tangent(g3,g4) = 1.5708
    c: Tangent(g0,g5) = 1.5708
    c: Tangent(g1,g5) = 1.5708
    c: Tangent(g1,g6) = 1.5708
    c: Tangent(g2,g6) = 1.5708
    c: Tangent(g2,g7) = 1.5708
    c: Tangent(g3,g7) = 1.5708
    c: Equal(g4,g5)
    c: DistanceY(g2,g0) = 25  'hauteur'
    c: DistanceX(g3,g1) = 25  'largeur'
    c: Equal(g5,g6)
    c: Equal(g6,g7)
    c: Radius(g7) = 2.5
    c: Symmetric(g1,g1,g-1)
    c: Symmetric(g0,g0,g-2)
    c: Coincident(g8,g9)
    c: Coincident(g9,g10)
    c: Coincident(g10,g11)
    c: Coincident(g11,g8)
    c: Horizontal(g10)
    c: Vertical(g11)
    c: Symmetric(g8,g9,g-1)
    c: Symmetric(g8,g8,g-2)
    c: DistanceX(g3,g8) = 2  'epaisseur'
    c: DistanceY(g2,g9) = 2
FEATURE [PartDesign::Pad] Pad013
  Direction = (1,1e-16,-1e-16)
  Length = 462
  Length2 = 100
  Placement = pos=(0,0,0) rot=(0.57735,0.57735,0.57735;2.0944rad)
  Profile = -> Sketch018
  Suppressed = false
  Type = 0
  expr: Length = Sketch014.Constraints.l2pied
FEATURE [Sketcher::SketchObject] Sketch030
  ArcFitTolerance = 1e-06
  AttachmentSupport = -> [YZ_Plane032]
  ExternalGeometry = -> [Pad013]
  FullyConstrained = false
  MakeInternals = false
  MapMode = 5
  Placement = pos=(0,0,0) rot=(0.57735,0.57735,0.57735;2.0944rad)
  sketch-geometry (5):
    g0: LineSegment StartX=12.5 StartY=17.5 StartZ=0 EndX=-57.5 EndY=17.5 EndZ=0
    g1: LineSegment StartX=-57.5 StartY=17.5 StartZ=0 EndX=-57.5 EndY=-17.5 EndZ=0
    g2: LineSegment StartX=-57.5 StartY=-17.5 StartZ=0 EndX=12.5 EndY=-17.5 EndZ=0
    g3: LineSegment StartX=12.5 StartY=-17.5 StartZ=0 EndX=12.5 EndY=17.5 EndZ=0
    g4: LineSegment [constr] StartX=12.5 StartY=37.849 StartZ=0 EndX=12.5 EndY=-63.3268 EndZ=0
  constraints (13):
    c: Coincident(g0,g1)
    c: Coincident(g1,g2)
    c: Coincident(g2,g3)
    c: Coincident(g3,g0)
    c: Horizontal(g0)
    c: Vertical(g3)
    c: Distance(g1,g3) = 70
    c: Distance(g0,g2) = 35
    c: Horizontal(g2)
    c: Symmetric(g0,g1,g-1)
    c: Vertical(g4)
    c: PointOnObject(g-3,g4)
    c: PointOnObject(g2,g4)
FEATURE [PartDesign::Groove] Groove004
  Angle = 59.9743
  Angle2 = 60
  Axis = (0,0,-101.176)
  Base = (0,12.5,37.849)
  BaseFeature = -> Pad013
  Placement = pos=(0,0,0) rot=(0.57735,0.57735,0.57735;2.0944rad)
  Profile = -> Sketch030
  ReferenceAxis = -> Sketch030 [Axis]
  Reversed = true
  Suppressed = false
  Type = 0
  expr: Angle = 90 ° - Sketch014.Constraints.angle2
FEATURE [PartDesign::Plane] DatumPlane002
  AttachmentSupport = -> [Groove004]
  Length = 60
  MapMode = 5
  Placement = pos=(462,2.033e-13,0) rot=(0.57735,0.57735,0.57735;2.0944rad)
  ResizeMode = 0
  Width = 60
FEATURE [Sketcher::SketchObject] Sketch031
  ArcFitTolerance = 1e-06
  AttachmentSupport = -> [DatumPlane002]
  ExternalGeometry = -> [Groove004]
  FullyConstrained = false
  MakeInternals = false
  MapMode = 5
  Placement = pos=(462,2.033e-13,0) rot=(0.57735,0.57735,0.57735;2.0944rad)
  sketch-geometry (5):
    g0: LineSegment [constr] StartX=12.5 StartY=67.6644 StartZ=0 EndX=12.5 EndY=-52.0571 EndZ=0
    g1: LineSegment StartX=-57.5 StartY=17.5 StartZ=0 EndX=-57.5 EndY=-17.5 EndZ=0
    g2: LineSegment StartX=-57.5 StartY=-17.5 StartZ=0 EndX=12.5 EndY=-17.5 EndZ=0
    g3: LineSegment StartX=12.5 StartY=-17.5 StartZ=0 EndX=12.5 EndY=17.5 EndZ=0
    g4: LineSegment StartX=12.5 StartY=17.5 StartZ=0 EndX=-57.5 EndY=17.5 EndZ=0
  constraints (13):
    c: Vertical(g0)
    c: Coincident(g1,g2)
    c: Coincident(g2,g3)
    c: Coincident(g3,g4)
    c: Coincident(g4,g1)
    c: Vertical(g3)
    c: Horizontal(g2)
    c: Horizontal(g4)
    c: Distance(g1,g3) = 70
    c: Distance(g2,g4) = 35
    c: PointOnObject(g3,g-3)
    c: PointOnObject(g0,g-3)
    c: Symmetric(g1,g1,g-1)
FEATURE [PartDesign::Groove] Groove005
  Angle = 30.0257
  Angle2 = 60
  Axis = (0,0,-119.722)
  Base = (462,12.5,67.6644)
  BaseFeature = -> Groove004
  Placement = pos=(0,0,0) rot=(0.57735,0.57735,0.57735;2.0944rad)
  Profile = -> Sketch031
  ReferenceAxis = -> Sketch031 [Axis]
  Suppressed = false
  Type = 0
  expr: Angle = Sketch014.Constraints.angle2
FEATURE [PartDesign::Body] Body011
  AllowCompound = false
  Group = -> [Pad013,Sketch018,Sketch030,Groove004,DatumPlane002,Sketch031,Groove005]
  Origin = -> Origin032
  Tip = -> Groove005
COMPONENT P16 — recipe-attached ("BB1", modeled in this document).
Construction recipe (the document's own serialized feature program — sketch geometry with constraints, then the solid features built on it; lengths are millimeters unless a unit is written):

FEATURE [Sketcher::SketchObject] Sketch019
  ArcFitTolerance = 0
  FullyConstrained = true
  MakeInternals = false
  MapMode = 5
  Placement = pos=(0,0,0) rot=(0.57735,0.57735,0.57735;2.0944rad)
  expr: Constraints[15] = .Constraints.hauteur * 0.1
  expr: Constraints[27] = .Constraints.epaisseur
  sketch-geometry (12):
    g0: LineSegment StartX=-10 StartY=12.5 StartZ=0 EndX=10 EndY=12.5 EndZ=0
    g1: LineSegment StartX=12.5 StartY=10 StartZ=0 EndX=12.5 EndY=-10 EndZ=0
    g2: LineSegment StartX=10 StartY=-12.5 StartZ=0 EndX=-10 EndY=-12.5 EndZ=0
    g3: LineSegment StartX=-12.5 StartY=-10 StartZ=0 EndX=-12.5 EndY=10 EndZ=0
    g4: ArcOfCircle CenterX=-10 CenterY=10 CenterZ=0 NormalX=0 NormalY=0 NormalZ=1 AngleXU=0 Radius=2.5 StartAngle=1.5708 EndAngle=3.14159
    g5: ArcOfCircle CenterX=10 CenterY=10 CenterZ=0 NormalX=0 NormalY=0 NormalZ=1 AngleXU=0 Radius=2.5 StartAngle=2e-16 EndAngle=1.5708
    g6: ArcOfCircle CenterX=10 CenterY=-10 CenterZ=0 NormalX=0 NormalY=0 NormalZ=1 AngleXU=0 Radius=2.5 StartAngle=4.71239 EndAngle=6.28319
    g7: ArcOfCircle CenterX=-10 CenterY=-10 CenterZ=0 NormalX=0 NormalY=0 NormalZ=1 AngleXU=0 Radius=2.5 StartAngle=3.14159 EndAngle=4.71239
    g8: LineSegment StartX=-10.5 StartY=10.5 StartZ=0 EndX=10.5 EndY=10.5 EndZ=0
    g9: LineSegment StartX=10.5 StartY=10.5 StartZ=0 EndX=10.5 EndY=-10.5 EndZ=0
    g10: LineSegment StartX=10.5 StartY=-10.5 StartZ=0 EndX=-10.5 EndY=-10.5 EndZ=0
    g11: LineSegment StartX=-10.5 StartY=-10.5 StartZ=0 EndX=-10.5 EndY=10.5 EndZ=0
  constraints (28):
    c: Horizontal(g2)
    c: Vertical(g3)
    c: Tangent(g0,g4) = 1.5708
    c: Tangent(g3,g4) = 1.5708
    c: Tangent(g0,g5) = 1.5708
    c: Tangent(g1,g5) = 1.5708
    c: Tangent(g1,g6) = 1.5708
    c: Tangent(g2,g6) = 1.5708
    c: Tangent(g2,g7) = 1.5708
    c: Tangent(g3,g7) = 1.5708
    c: Equal(g4,g5)
    c: DistanceY(g2,g0) = 25  'hauteur'
    c: DistanceX(g3,g1) = 25  'largeur'
    c: Equal(g5,g6)
    c: Equal(g6,g7)
    c: Radius(g7) = 2.5
    c: Symmetric(g1,g1,g-1)
    c: Symmetric(g0,g0,g-2)
    c: Coincident(g8,g9)
    c: Coincident(g9,g10)
    c: Coincident(g10,g11)
    c: Coincident(g11,g8)
    c: Horizontal(g10)
    c: Vertical(g11)
    c: Symmetric(g8,g9,g-1)
    c: Symmetric(g8,g8,g-2)
    c: DistanceX(g3,g8) = 2  'epaisseur'
    c: DistanceY(g2,g9) = 2
FEATURE [PartDesign::Pad] Pad014
  Direction = (1,1e-16,-1e-16)
  Length = 685
  Length2 = 100
  Placement = pos=(0,0,0) rot=(0.57735,0.57735,0.57735;2.0944rad)
  Profile = -> Sketch019
  Suppressed = false
  Type = 0
  expr: Length = Spreadsheet.B12 + Spreadsheet.B2 * 3
FEATURE [PartDesign::Body] Body012
  AllowCompound = false
  Group = -> [Sketch019,Pad014]
  Origin = -> Origin034
  Tip = -> Pad014
COMPONENT P17 — recipe-attached ("BB2", modeled in this document).
Construction recipe (the document's own serialized feature program — sketch geometry with constraints, then the solid features built on it; lengths are millimeters unless a unit is written):

FEATURE [Sketcher::SketchObject] Sketch020
  ArcFitTolerance = 0
  FullyConstrained = true
  MakeInternals = false
  MapMode = 5
  Placement = pos=(0,0,0) rot=(0.57735,0.57735,0.57735;2.0944rad)
  expr: Constraints[15] = .Constraints.hauteur * 0.1
  expr: Constraints[27] = .Constraints.epaisseur
  sketch-geometry (12):
    g0: LineSegment StartX=-10 StartY=12.5 StartZ=0 EndX=10 EndY=12.5 EndZ=0
    g1: LineSegment StartX=12.5 StartY=10 StartZ=0 EndX=12.5 EndY=-10 EndZ=0
    g2: LineSegment StartX=10 StartY=-12.5 StartZ=0 EndX=-10 EndY=-12.5 EndZ=0
    g3: LineSegment StartX=-12.5 StartY=-10 StartZ=0 EndX=-12.5 EndY=10 EndZ=0
    g4: ArcOfCircle CenterX=-10 CenterY=10 CenterZ=0 NormalX=0 NormalY=0 NormalZ=1 AngleXU=0 Radius=2.5 StartAngle=1.5708 EndAngle=3.14159
    g5: ArcOfCircle CenterX=10 CenterY=10 CenterZ=0 NormalX=0 NormalY=0 NormalZ=1 AngleXU=0 Radius=2.5 StartAngle=2e-16 EndAngle=1.5708
    g6: ArcOfCircle CenterX=10 CenterY=-10 CenterZ=0 NormalX=0 NormalY=0 NormalZ=1 AngleXU=0 Radius=2.5 StartAngle=4.71239 EndAngle=6.28319
    g7: ArcOfCircle CenterX=-10 CenterY=-10 CenterZ=0 NormalX=0 NormalY=0 NormalZ=1 AngleXU=0 Radius=2.5 StartAngle=3.14159 EndAngle=4.71239
    g8: LineSegment StartX=-10.5 StartY=10.5 StartZ=0 EndX=10.5 EndY=10.5 EndZ=0
    g9: LineSegment StartX=10.5 StartY=10.5 StartZ=0 EndX=10.5 EndY=-10.5 EndZ=0
    g10: LineSegment StartX=10.5 StartY=-10.5 StartZ=0 EndX=-10.5 EndY=-10.5 EndZ=0
    g11: LineSegment StartX=-10.5 StartY=-10.5 StartZ=0 EndX=-10.5 EndY=10.5 EndZ=0
  constraints (28):
    c: Horizontal(g2)
    c: Vertical(g3)
    c: Tangent(g0,g4) = 1.5708
    c: Tangent(g3,g4) = 1.5708
    c: Tangent(g0,g5) = 1.5708
    c: Tangent(g1,g5) = 1.5708
    c: Tangent(g1,g6) = 1.5708
    c: Tangent(g2,g6) = 1.5708
    c: Tangent(g2,g7) = 1.5708
    c: Tangent(g3,g7) = 1.5708
    c: Equal(g4,g5)
    c: DistanceY(g2,g0) = 25  'hauteur'
    c: DistanceX(g3,g1) = 25  'largeur'
    c: Equal(g5,g6)
    c: Equal(g6,g7)
    c: Radius(g7) = 2.5
    c: Symmetric(g1,g1,g-1)
    c: Symmetric(g0,g0,g-2)
    c: Coincident(g8,g9)
    c: Coincident(g9,g10)
    c: Coincident(g10,g11)
    c: Coincident(g11,g8)
    c: Horizontal(g10)
    c: Vertical(g11)
    c: Symmetric(g8,g9,g-1)
    c: Symmetric(g8,g8,g-2)
    c: DistanceX(g3,g8) = 2  'epaisseur'
    c: DistanceY(g2,g9) = 2
FEATURE [PartDesign::Pad] Pad015
  Direction = (1,1e-16,-1e-16)
  Length = 560
  Length2 = 100
  Placement = pos=(0,0,0) rot=(0.57735,0.57735,0.57735;2.0944rad)
  Profile = -> Sketch020
  Suppressed = false
  Type = 0
  expr: Length = Spreadsheet.B12 - Spreadsheet.B2 * 2
FEATURE [PartDesign::Body] Body013
  AllowCompound = false
  Group = -> [Sketch020,Pad015]
  Origin = -> Origin036
  Tip = -> Pad015
COMPONENT P18 — recipe-attached ("BB3", modeled in this document).
Construction recipe (the document's own serialized feature program — sketch geometry with constraints, then the solid features built on it; lengths are millimeters unless a unit is written):

FEATURE [Sketcher::SketchObject] Sketch021
  ArcFitTolerance = 0
  FullyConstrained = true
  MakeInternals = false
  MapMode = 5
  Placement = pos=(0,0,0) rot=(0.57735,0.57735,0.57735;2.0944rad)
  expr: Constraints[15] = .Constraints.hauteur * 0.1
  expr: Constraints[27] = .Constraints.epaisseur
  sketch-geometry (12):
    g0: LineSegment StartX=-10 StartY=12.5 StartZ=0 EndX=10 EndY=12.5 EndZ=0
    g1: LineSegment StartX=12.5 StartY=10 StartZ=0 EndX=12.5 EndY=-10 EndZ=0
    g2: LineSegment StartX=10 StartY=-12.5 StartZ=0 EndX=-10 EndY=-12.5 EndZ=0
    g3: LineSegment StartX=-12.5 StartY=-10 StartZ=0 EndX=-12.5 EndY=10 EndZ=0
    g4: ArcOfCircle CenterX=-10 CenterY=10 CenterZ=0 NormalX=0 NormalY=0 NormalZ=1 AngleXU=0 Radius=2.5 StartAngle=1.5708 EndAngle=3.14159
    g5: ArcOfCircle CenterX=10 CenterY=10 CenterZ=0 NormalX=0 NormalY=0 NormalZ=1 AngleXU=0 Radius=2.5 StartAngle=2e-16 EndAngle=1.5708
    g6: ArcOfCircle CenterX=10 CenterY=-10 CenterZ=0 NormalX=0 NormalY=0 NormalZ=1 AngleXU=0 Radius=2.5 StartAngle=4.71239 EndAngle=6.28319
    g7: ArcOfCircle CenterX=-10 CenterY=-10 CenterZ=0 NormalX=0 NormalY=0 NormalZ=1 AngleXU=0 Radius=2.5 StartAngle=3.14159 EndAngle=4.71239
    g8: LineSegment StartX=-10.5 StartY=10.5 StartZ=0 EndX=10.5 EndY=10.5 EndZ=0
    g9: LineSegment StartX=10.5 StartY=10.5 StartZ=0 EndX=10.5 EndY=-10.5 EndZ=0
    g10: LineSegment StartX=10.5 StartY=-10.5 StartZ=0 EndX=-10.5 EndY=-10.5 EndZ=0
    g11: LineSegment StartX=-10.5 StartY=-10.5 StartZ=0 EndX=-10.5 EndY=10.5 EndZ=0
  constraints (28):
    c: Horizontal(g2)
    c: Vertical(g3)
    c: Tangent(g0,g4) = 1.5708
    c: Tangent(g3,g4) = 1.5708
    c: Tangent(g0,g5) = 1.5708
    c: Tangent(g1,g5) = 1.5708
    c: Tangent(g1,g6) = 1.5708
    c: Tangent(g2,g6) = 1.5708
    c: Tangent(g2,g7) = 1.5708
    c: Tangent(g3,g7) = 1.5708
    c: Equal(g4,g5)
    c: DistanceY(g2,g0) = 25  'hauteur'
    c: DistanceX(g3,g1) = 25  'largeur'
    c: Equal(g5,g6)
    c: Equal(g6,g7)
    c: Radius(g7) = 2.5
    c: Symmetric(g1,g1,g-1)
    c: Symmetric(g0,g0,g-2)
    c: Coincident(g8,g9)
    c: Coincident(g9,g10)
    c: Coincident(g10,g11)
    c: Coincident(g11,g8)
    c: Horizontal(g10)
    c: Vertical(g11)
    c: Symmetric(g8,g9,g-1)
    c: Symmetric(g8,g8,g-2)
    c: DistanceX(g3,g8) = 2  'epaisseur'
    c: DistanceY(g2,g9) = 2
FEATURE [PartDesign::Pad] Pad016
  Direction = (1,1e-16,-1e-16)
  Length = 610
  Length2 = 100
  Placement = pos=(0,0,0) rot=(0.57735,0.57735,0.57735;2.0944rad)
  Profile = -> Sketch021
  Suppressed = false
  Type = 0
  expr: Length = Spreadsheet.D4
FEATURE [PartDesign::Body] Body014
  AllowCompound = false
  Group = -> [Sketch021,Pad016]
  Origin = -> Origin038
  Tip = -> Pad016
COMPONENT P19 — recipe-attached ("A16", modeled in this document).
Construction recipe (the document's own serialized feature program — sketch geometry with constraints, then the solid features built on it; lengths are millimeters unless a unit is written):

FEATURE [Sketcher::SketchObject] Sketch022
  ArcFitTolerance = 0
  FullyConstrained = true
  MakeInternals = false
  MapMode = 5
  Placement = pos=(0,0,0) rot=(0.57735,0.57735,0.57735;2.0944rad)
  expr: Constraints[15] = .Constraints.hauteur * 0.1
  expr: Constraints[27] = .Constraints.epaisseur
  sketch-geometry (12):
    g0: LineSegment StartX=-12 StartY=15 StartZ=0 EndX=12 EndY=15 EndZ=0
    g1: LineSegment StartX=15 StartY=12 StartZ=0 EndX=15 EndY=-12 EndZ=0
    g2: LineSegment StartX=12 StartY=-15 StartZ=0 EndX=-12 EndY=-15 EndZ=0
    g3: LineSegment StartX=-15 StartY=-12 StartZ=0 EndX=-15 EndY=12 EndZ=0
    g4: ArcOfCircle CenterX=-12 CenterY=12 CenterZ=0 NormalX=0 NormalY=0 NormalZ=1 AngleXU=0 Radius=3 StartAngle=1.5708 EndAngle=3.14159
    g5: ArcOfCircle CenterX=12 CenterY=12 CenterZ=0 NormalX=0 NormalY=0 NormalZ=1 AngleXU=0 Radius=3 StartAngle=1e-16 EndAngle=1.5708
    g6: ArcOfCircle CenterX=12 CenterY=-12 CenterZ=0 NormalX=0 NormalY=0 NormalZ=1 AngleXU=0 Radius=3 StartAngle=4.71239 EndAngle=6.28319
    g7: ArcOfCircle CenterX=-12 CenterY=-12 CenterZ=0 NormalX=0 NormalY=0 NormalZ=1 AngleXU=0 Radius=3 StartAngle=3.14159 EndAngle=4.71239
    g8: LineSegment StartX=-13 StartY=13 StartZ=0 EndX=13 EndY=13 EndZ=0
    g9: LineSegment StartX=13 StartY=13 StartZ=0 EndX=13 EndY=-13 EndZ=0
    g10: LineSegment StartX=13 StartY=-13 StartZ=0 EndX=-13 EndY=-13 EndZ=0
    g11: LineSegment StartX=-13 StartY=-13 StartZ=0 EndX=-13 EndY=13 EndZ=0
  constraints (28):
    c: Horizontal(g2)
    c: Vertical(g3)
    c: Tangent(g0,g4) = 1.5708
    c: Tangent(g3,g4) = 1.5708
    c: Tangent(g0,g5) = 1.5708
    c: Tangent(g1,g5) = 1.5708
    c: Tangent(g1,g6) = 1.5708
    c: Tangent(g2,g6) = 1.5708
    c: Tangent(g2,g7) = 1.5708
    c: Tangent(g3,g7) = 1.5708
    c: Equal(g4,g5)
    c: DistanceY(g2,g0) = 30  'hauteur'
    c: DistanceX(g3,g1) = 30  'largeur'
    c: Equal(g5,g6)
    c: Equal(g6,g7)
    c: Radius(g7) = 3
    c: Symmetric(g1,g1,g-1)
    c: Symmetric(g0,g0,g-2)
    c: Coincident(g8,g9)
    c: Coincident(g9,g10)
    c: Coincident(g10,g11)
    c: Coincident(g11,g8)
    c: Horizontal(g10)
    c: Vertical(g11)
    c: Symmetric(g8,g9,g-1)
    c: Symmetric(g8,g8,g-2)
    c: DistanceX(g3,g8) = 2  'epaisseur'
    c: DistanceY(g2,g9) = 2
FEATURE [PartDesign::Pad] Pad017
  Direction = (1,1e-16,-1e-16)
  Length = 50
  Length2 = 100
  Placement = pos=(0,0,0) rot=(0.57735,0.57735,0.57735;2.0944rad)
  Profile = -> Sketch022
  Suppressed = false
  Type = 0
  expr: Length = 2 * Spreadsheet.B2
FEATURE [PartDesign::Body] Body015
  AllowCompound = false
  Group = -> [Sketch022,Pad017]
  Origin = -> Origin040
  Tip = -> Pad017
COMPONENT P20 — recipe-attached ("A17", modeled in this document).
Construction recipe (the document's own serialized feature program — sketch geometry with constraints, then the solid features built on it; lengths are millimeters unless a unit is written):

FEATURE [Sketcher::SketchObject] Sketch024
  ArcFitTolerance = 0
  AttachmentSupport = -> [XZ_Plane042]
  FullyConstrained = true
  MakeInternals = false
  MapMode = 5
  Placement = pos=(0,0,0) rot=(1,0,0;1.5708rad)
  expr: .Constraints.diametre = Spreadsheet.B13
  sketch-geometry (4):
    g0: Circle CenterX=0 CenterY=0 CenterZ=0 NormalX=0 NormalY=0 NormalZ=1 AngleXU=0 Radius=13
    g1: Circle CenterX=0 CenterY=0 CenterZ=0 NormalX=0 NormalY=0 NormalZ=1 AngleXU=0 Radius=15
    g2: GeomPoint [constr] X=-15 Y=0 Z=0
    g3: GeomPoint [constr] X=-13 Y=0 Z=0
  constraints (8):
    c: Coincident(g1,g0)
    c: PointOnObject(g2,g1)
    c: PointOnObject(g3,g0)
    c: Coincident(g0,g-1)
    c: PointOnObject(g3,g-1)
    c: PointOnObject(g2,g-1)
    c: DistanceX(g2,g3) = 2  'epaisseur'
    c: Diameter(g1) = 30  'diametre'
FEATURE [PartDesign::Pad] Pad018
  Direction = (0,-1,2e-16)
  Length = 300
  Length2 = 100
  Placement = pos=(0,0,0) rot=(1,0,0;1.5708rad)
  Profile = -> Sketch024
  Suppressed = false
  Type = 0
FEATURE [PartDesign::Body] Body016
  AllowCompound = false
  Group = -> [Sketch024,Pad018]
  Origin = -> Origin042
  Tip = -> Pad018
COMPONENT P21 — recipe-attached ("A18", modeled in this document).
Construction recipe (the document's own serialized feature program — sketch geometry with constraints, then the solid features built on it; lengths are millimeters unless a unit is written):

FEATURE [Sketcher::SketchObject] Sketch025
  ArcFitTolerance = 0
  FullyConstrained = true
  MakeInternals = false
  MapMode = 5
  Placement = pos=(0,0,0) rot=(0.57735,0.57735,0.57735;2.0944rad)
  expr: Constraints[15] = .Constraints.hauteur * 0.1
  expr: Constraints[27] = .Constraints.epaisseur
  sketch-geometry (12):
    g0: LineSegment StartX=-10 StartY=12.5 StartZ=0 EndX=10 EndY=12.5 EndZ=0
    g1: LineSegment StartX=12.5 StartY=10 StartZ=0 EndX=12.5 EndY=-10 EndZ=0
    g2: LineSegment StartX=10 StartY=-12.5 StartZ=0 EndX=-10 EndY=-12.5 EndZ=0
    g3: LineSegment StartX=-12.5 StartY=-10 StartZ=0 EndX=-12.5 EndY=10 EndZ=0
    g4: ArcOfCircle CenterX=-10 CenterY=10 CenterZ=0 NormalX=0 NormalY=0 NormalZ=1 AngleXU=0 Radius=2.5 StartAngle=1.5708 EndAngle=3.14159
    g5: ArcOfCircle CenterX=10 CenterY=10 CenterZ=0 NormalX=0 NormalY=0 NormalZ=1 AngleXU=0 Radius=2.5 StartAngle=2e-16 EndAngle=1.5708
    g6: ArcOfCircle CenterX=10 CenterY=-10 CenterZ=0 NormalX=0 NormalY=0 NormalZ=1 AngleXU=0 Radius=2.5 StartAngle=4.71239 EndAngle=6.28319
    g7: ArcOfCircle CenterX=-10 CenterY=-10 CenterZ=0 NormalX=0 NormalY=0 NormalZ=1 AngleXU=0 Radius=2.5 StartAngle=3.14159 EndAngle=4.71239
    g8: LineSegment StartX=-10.5 StartY=10.5 StartZ=0 EndX=10.5 EndY=10.5 EndZ=0
    g9: LineSegment StartX=10.5 StartY=10.5 StartZ=0 EndX=10.5 EndY=-10.5 EndZ=0
    g10: LineSegment StartX=10.5 StartY=-10.5 StartZ=0 EndX=-10.5 EndY=-10.5 EndZ=0
    g11: LineSegment StartX=-10.5 StartY=-10.5 StartZ=0 EndX=-10.5 EndY=10.5 EndZ=0
  constraints (28):
    c: Horizontal(g2)
    c: Vertical(g3)
    c: Tangent(g0,g4) = 1.5708
    c: Tangent(g3,g4) = 1.5708
    c: Tangent(g0,g5) = 1.5708
    c: Tangent(g1,g5) = 1.5708
    c: Tangent(g1,g6) = 1.5708
    c: Tangent(g2,g6) = 1.5708
    c: Tangent(g2,g7) = 1.5708
    c: Tangent(g3,g7) = 1.5708
    c: Equal(g4,g5)
    c: DistanceY(g2,g0) = 25  'hauteur'
    c: DistanceX(g3,g1) = 25  'largeur'
    c: Equal(g5,g6)
    c: Equal(g6,g7)
    c: Radius(g7) = 2.5
    c: Symmetric(g1,g1,g-1)
    c: Symmetric(g0,g0,g-2)
    c: Coincident(g8,g9)
    c: Coincident(g9,g10)
    c: Coincident(g10,g11)
    c: Coincident(g11,g8)
    c: Horizontal(g10)
    c: Vertical(g11)
    c: Symmetric(g8,g9,g-1)
    c: Symmetric(g8,g8,g-2)
    c: DistanceX(g3,g8) = 2  'epaisseur'
    c: DistanceY(g2,g9) = 2
FEATURE [PartDesign::Pad] Pad019
  Direction = (1,1e-16,-1e-16)
  Length = 142
  Length2 = 100
  Placement = pos=(0,0,0) rot=(0.57735,0.57735,0.57735;2.0944rad)
  Profile = -> Sketch025
  Suppressed = false
  Type = 0
FEATURE [Sketcher::SketchObject] Sketch026
  ArcFitTolerance = 1e-06
  AttachmentSupport = -> [YZ_Plane044]
  ExternalGeometry = -> [Pad019]
  FullyConstrained = false
  MakeInternals = false
  MapMode = 5
  Placement = pos=(0,0,0) rot=(0.57735,0.57735,0.57735;2.0944rad)
  sketch-geometry (5):
    g0: LineSegment [constr] StartX=-12.5 StartY=34.6544 StartZ=0 EndX=-12.5 EndY=-40.7923 EndZ=0
    g1: LineSegment StartX=-12.5 StartY=-17.5 StartZ=0 EndX=57.5 EndY=-17.5 EndZ=0
    g2: LineSegment StartX=57.5 StartY=-17.5 StartZ=0 EndX=57.5 EndY=17.5 EndZ=0
    g3: LineSegment StartX=57.5 StartY=17.5 StartZ=0 EndX=-12.5 EndY=17.5 EndZ=0
    g4: LineSegment StartX=-12.5 StartY=17.5 StartZ=0 EndX=-12.5 EndY=-17.5 EndZ=0
  constraints (13):
    c: Coincident(g1,g2)
    c: Coincident(g2,g3)
    c: Coincident(g3,g4)
    c: Coincident(g4,g1)
    c: Horizontal(g3)
    c: Vertical(g2)
    c: Distance(g2,g4) = 70
    c: Distance(g1,g3) = 35
    c: Vertical(g0)
    c: PointOnObject(g-3,g0)
    c: Symmetric(g3,g1,g-1)
    c: PointOnObject(g3,g0)
    c: Horizontal(g1)
FEATURE [PartDesign::Plane] DatumPlane
  AttachmentSupport = -> [Pad019]
  Length = 60
  MapMode = 5
  Placement = pos=(142,6.25e-14,0) rot=(0.57735,0.57735,0.57735;2.0944rad)
  ResizeMode = 0
  Width = 60
FEATURE [Sketcher::SketchObject] Sketch027
  ArcFitTolerance = 1e-06
  AttachmentSupport = -> [DatumPlane]
  ExternalGeometry = -> [Pad019]
  FullyConstrained = false
  MakeInternals = false
  MapMode = 5
  Placement = pos=(142,6.25e-14,0) rot=(0.57735,0.57735,0.57735;2.0944rad)
  sketch-geometry (5):
    g0: LineSegment [constr] StartX=-12.5 StartY=-38.9997 StartZ=0 EndX=-12.5 EndY=36.6406 EndZ=0
    g1: LineSegment StartX=-12.5 StartY=-17.5 StartZ=0 EndX=57.5 EndY=-17.5 EndZ=0
    g2: LineSegment StartX=57.5 StartY=-17.5 StartZ=0 EndX=57.5 EndY=17.5 EndZ=0
    g3: LineSegment StartX=57.5 StartY=17.5 StartZ=0 EndX=-12.5 EndY=17.5 EndZ=0
    g4: LineSegment StartX=-12.5 StartY=17.5 StartZ=0 EndX=-12.5 EndY=-17.5 EndZ=0
  constraints (13):
    c: Coincident(g1,g2)
    c: Coincident(g2,g3)
    c: Coincident(g3,g4)
    c: Coincident(g4,g1)
    c: Horizontal(g3)
    c: Vertical(g2)
    c: Distance(g2,g4) = 70
    c: Distance(g1,g3) = 35
    c: PointOnObject(g0,g-4)
    c: Vertical(g0)
    c: Symmetric(g3,g1,g-1)
    c: Horizontal(g1)
    c: PointOnObject(g1,g0)
FEATURE [PartDesign::Groove] Groove
  Angle = 45
  Angle2 = 60
  Axis = (0,0,-75.4468)
  Base = (0,-12.5,34.6544)
  BaseFeature = -> Pad019
  Placement = pos=(0,0,0) rot=(0.57735,0.57735,0.57735;2.0944rad)
  Profile = -> Sketch026
  ReferenceAxis = -> Sketch026 [Axis]
  Suppressed = false
  Type = 0
FEATURE [PartDesign::Groove] Groove001
  Angle = 45
  Angle2 = 60
  Axis = (0,0,75.6403)
  Base = (142,-12.5,-38.9997)
  BaseFeature = -> Groove
  Placement = pos=(0,0,0) rot=(0.57735,0.57735,0.57735;2.0944rad)
  Profile = -> Sketch027
  ReferenceAxis = -> Sketch027 [Axis]
  Suppressed = false
  Type = 0
FEATURE [PartDesign::Body] Body017
  AllowCompound = false
  Group = -> [Sketch025,Pad019,Sketch026,DatumPlane,Sketch027,Groove,Groove001]
  Origin = -> Origin044
  Tip = -> Groove001
COMPONENT P22 — recipe-attached ("Roue_increvable___389___axe25_L_82", modeled in this document).
Construction recipe (the document's own serialized feature program — sketch geometry with constraints, then the solid features built on it; lengths are millimeters unless a unit is written):

FEATURE [Sketcher::SketchObject] Sketch005
  ArcFitTolerance = 0
  AttachmentSupport = -> [XY_Plane010]
  FullyConstrained = true
  MakeInternals = false
  MapMode = 5
  sketch-geometry (16):
    g0: LineSegment StartX=-41 StartY=12.5 StartZ=0 EndX=41 EndY=12.5 EndZ=0
    g1: LineSegment StartX=-41 StartY=12.5 StartZ=0 EndX=-41 EndY=17.5 EndZ=0
    g2: LineSegment StartX=-41 StartY=17.5 StartZ=0 EndX=-38 EndY=17.5 EndZ=0
    g3: LineSegment StartX=-38 StartY=17.5 StartZ=0 EndX=-38 EndY=120 EndZ=0
    g4: LineSegment StartX=-38 StartY=120 StartZ=0 EndX=-36 EndY=120 EndZ=0
    g5: LineSegment StartX=-36 StartY=120 StartZ=0 EndX=-36 EndY=122 EndZ=0
    g6: LineSegment StartX=-36 StartY=122 StartZ=0 EndX=-38 EndY=122 EndZ=0
    g7: LineSegment StartX=41 StartY=12.5 StartZ=0 EndX=41 EndY=17.5 EndZ=0
    g8: LineSegment StartX=41 StartY=17.5 StartZ=0 EndX=38 EndY=17.5 EndZ=0
    g9: LineSegment StartX=38 StartY=17.5 StartZ=0 EndX=38 EndY=120 EndZ=0
    g10: LineSegment StartX=38 StartY=120 StartZ=0 EndX=36 EndY=120 EndZ=0
    g11: LineSegment StartX=36 StartY=120 StartZ=0 EndX=36 EndY=122 EndZ=0
    g12: LineSegment StartX=36 StartY=122 StartZ=0 EndX=38 EndY=122 EndZ=0
    g13: GeomPoint [constr] X=-1e-15 Y=151.744 Z=0
    g14: GeomPoint [constr] X=0 Y=200 Z=0
    g15: ArcOfCircle CenterX=-1e-15 CenterY=151.744 CenterZ=0 NormalX=0 NormalY=0 NormalZ=1 AngleXU=0 Radius=48.2564 StartAngle=5.61907 EndAngle=10.0889
  constraints (42):
    c: Symmetric(g0,g0,g-2)
    c: Coincident(g0,g1)
    c: Vertical(g1)
    c: Coincident(g1,g2)
    c: Horizontal(g2)
    c: Coincident(g2,g3)
    c: Vertical(g3)
    c: Coincident(g3,g4)
    c: Horizontal(g4)
    c: Coincident(g4,g5)
    c: Coincident(g5,g6)
    c: Horizontal(g6)
    c: Vertical(g5)
    c: PointOnObject(g6,g3)
    c: DistanceX(g2,g2) = 3
    c: DistanceX(g4,g4) = 2
    c: DistanceY(g5,g5) = 2
    c: Vertical(g7)
    c: Coincident(g7,g8)
    c: Horizontal(g8)
    c: Coincident(g8,g9)
    c: Coincident(g9,g10)
    c: Horizontal(g10)
    c: Coincident(g10,g11)
    c: Coincident(g11,g12)
    c: Horizontal(g12)
    c: Vertical(g11)
    c: PointOnObject(g12,g9)
    c: Symmetric(g9,g3,g-2)
    c: Symmetric(g5,g11,g-2)
    c: DistanceX(g2,g8) = 76
    c: Coincident(g0,g7)
    c: DistanceY(g-1,g0) = 12.5
    c: DistanceY(g7,g7) = 5
    c: Symmetric(g2,g8,g-2)
    c: PointOnObject(g14,g-2)
    c: DistanceY(g-1,g9) = 120
    c: DistanceY(g-1,g14) = 200
    c: Coincident(g15,g13)
    c: Coincident(g15,g6)
    c: Coincident(g15,g12)
    c: PointOnObject(g14,g15)
FEATURE [PartDesign::Revolution] Revolution
  Angle = 360
  Angle2 = 60
  Axis = (1,0,0)
  Base = (0,0,0)
  Profile = -> Sketch005
  ReferenceAxis = -> Sketch005 [H_Axis]
  Suppressed = false
  Type = 0
FEATURE [PartDesign::Body] Body004
  AllowCompound = false
  Group = -> [Sketch005,Revolution]
  Origin = -> Origin010
  Tip = -> Revolution
COMPONENT P23 — recipe-attached ("goupille elastique 5 x 80", modeled in this document).
Construction recipe (the document's own serialized feature program — sketch geometry with constraints, then the solid features built on it; lengths are millimeters unless a unit is written):

FEATURE [PartDesign::CoordinateSystem] LCS_Origin004
  AttacherType = Attacher::AttachEngine3D
  AttachmentSupport = -> [X_Axis050]
  MapMode = 2
FEATURE [Sketcher::SketchObject] Sketch036
  ArcFitTolerance = 1e-06
  AttachmentSupport = -> [XZ_Plane048]
  FullyConstrained = false
  MakeInternals = false
  MapMode = 5
  Placement = pos=(0,0,0) rot=(1,0,0;1.5708rad)
  sketch-geometry (11):
    g0: Circle [constr] CenterX=0 CenterY=0 CenterZ=0 NormalX=0 NormalY=0 NormalZ=1 AngleXU=0 Radius=13.75
    g1: LineSegment [constr] StartX=0 StartY=-40 StartZ=0 EndX=0 EndY=40 EndZ=0
    g2: Circle [constr] CenterX=-10 CenterY=30 CenterZ=0 NormalX=0 NormalY=0 NormalZ=1 AngleXU=0 Radius=10
    g3: GeomPoint [constr] X=0 Y=30 Z=0
    g4: LineSegment [constr] StartX=0 StartY=40 StartZ=0 EndX=-69.1627 EndY=40 EndZ=0
    g5: LineSegment StartX=0 StartY=-40 StartZ=0 EndX=0 EndY=30 EndZ=0
    g6: ArcOfCircle CenterX=-10 CenterY=30 CenterZ=0 NormalX=0 NormalY=0 NormalZ=1 AngleXU=0 Radius=10 StartAngle=4.06135e-09 EndAngle=4.58938
    g7: ArcOfCircle CenterX=-11.8728 CenterY=14.8514 CenterZ=0 NormalX=0 NormalY=0 NormalZ=1 AngleXU=0 Radius=5.26396 StartAngle=5.38202 EndAngle=7.73097
    g8: ArcOfCircle CenterX=0 CenterY=0 CenterZ=0 NormalX=0 NormalY=0 NormalZ=1 AngleXU=0 Radius=13.75 StartAngle=2.24702 EndAngle=4.04719
    g9: ArcOfCircle CenterX=-12.0115 CenterY=-15.2346 CenterZ=0 NormalX=0 NormalY=0 NormalZ=1 AngleXU=0 Radius=5.65039 StartAngle=5.15136 EndAngle=7.18037
    g10: LineSegment StartX=-9.61003 StartY=-20.3493 StartZ=0 EndX=-12.9682 EndY=-21.926 EndZ=0
  constraints (21):
    c: Diameter(g0) = 27.5
    c: Coincident(g0,g-1)
    c: Distance(g1) = 80
    c: Vertical(g1)
    c: Diameter(g2) = 20
    c: PointOnObject(g3,g2)
    c: PointOnObject(g3,g1)
    c: Coincident(g4,g1)
    c: Horizontal(g4)
    c: Tangent(g4,g2)
    c: Symmetric(g1,g1,g0)
    c: Coincident(g5,g1)
    c: Coincident(g5,g3)
    c: Coincident(g6,g2)
    c: Coincident(g6,g3)
    c: PointOnObject(g7,g0)
    c: Coincident(g7,g6)
    c: Coincident(g8,g0)
    c: Coincident(g8,g7)
    c: Coincident(g9,g8)
    c: Tangent(g10,g9) = 1.5708
FEATURE [PartDesign::Plane] DatumPlane005
  AttachmentSupport = -> [Sketch036]
  Length = 60
  MapMode = 7
  Placement = pos=(0,-8.9e-15,-40) rot=(0,1,0;3.14159rad)
  ResizeMode = 0
  Width = 60
FEATURE [Sketcher::SketchObject] Sketch037
  ArcFitTolerance = 1e-06
  AttachmentSupport = -> [DatumPlane005]
  FullyConstrained = true
  MakeInternals = false
  MapMode = 5
  Placement = pos=(0,-8.9e-15,-40) rot=(0,1,0;3.14159rad)
  sketch-geometry (1):
    g0: Circle CenterX=0 CenterY=0 CenterZ=0 NormalX=0 NormalY=0 NormalZ=1 AngleXU=0 Radius=2.5
  constraints (2):
    c: Diameter(g0) = 5
    c: Coincident(g0,g-1)
FEATURE [PartDesign::AdditivePipe] AdditivePipe001
  AuxilleryCurvelinear = true
  AuxillerySpineTangent = false
  Binormal = (0,0,0)
  Mode = 0
  Placement = pos=(0,-8.9e-15,-40) rot=(0,1,0;3.14159rad)
  Profile = -> Sketch037
  Spine = -> Sketch036
  SpineTangent = false
  Suppressed = false
  Transformation = 0
  Transition = 0
FEATURE [PartDesign::Body] goupille
  AllowCompound = false
  Group = -> [LCS_Origin004,Sketch036,DatumPlane005,Sketch037,AdditivePipe001]
  Origin = -> Origin048
  Tip = -> AdditivePipe001
COMPONENT P24 — recipe-attached ("rondelle 25", modeled in this document).
Construction recipe (the document's own serialized feature program — sketch geometry with constraints, then the solid features built on it; lengths are millimeters unless a unit is written):

FEATURE [PartDesign::CoordinateSystem] LCS_Origin002
  AttacherType = Attacher::AttachEngine3D
  AttachmentSupport = -> [X_Axis048]
  MapMode = 2
FEATURE [Sketcher::SketchObject] Sketch035
  ArcFitTolerance = 1e-06
  AttachmentSupport = -> [YZ_Plane046]
  FullyConstrained = true
  MakeInternals = false
  MapMode = 5
  Placement = pos=(0,0,0) rot=(0.57735,0.57735,0.57735;2.0944rad)
  sketch-geometry (4):
    g0: LineSegment StartX=-1 StartY=28 StartZ=0 EndX=-1 EndY=13 EndZ=0
    g1: LineSegment StartX=-1 StartY=13 StartZ=0 EndX=1 EndY=13 EndZ=0
    g2: LineSegment StartX=1 StartY=13 StartZ=0 EndX=1 EndY=28 EndZ=0
    g3: LineSegment StartX=1 StartY=28 StartZ=0 EndX=-1 EndY=28 EndZ=0
  constraints (11):
    c: Coincident(g0,g1)
    c: Coincident(g1,g2)
    c: Coincident(g2,g3)
    c: Coincident(g3,g0)
    c: Vertical(g0)
    c: Vertical(g2)
    c: Horizontal(g3)
    c: Symmetric(g0,g1,g-2)
    c: DistanceY(g-1,g1) = 13  'rayint'
    c: DistanceY(g-1,g2) = 28  'rayext'
    c: DistanceX(g3,g3) = 2  'ep'
FEATURE [PartDesign::Revolution] Revolution001
  Angle = 360
  Angle2 = 60
  Axis = (0,1,0)
  Base = (0,0,0)
  Placement = pos=(0,0,0) rot=(1,1,1;2.0944rad)
  Profile = -> Sketch035
  ReferenceAxis = -> Sketch035 [H_Axis]
  Suppressed = false
  Type = 0
FEATURE [PartDesign::Body] rondellle
  AllowCompound = false
  Group = -> [LCS_Origin002,Sketch035,Revolution001]
  Origin = -> Origin046
  Tip = -> Revolution001
PROVENANCE & LICENSES
A FreeCAD (.FCStd) document from a public repository crawl; recipes are the document's own serialized feature recipes (and, for linked parts, companion documents' recipes).
License: gpl-3.0.
